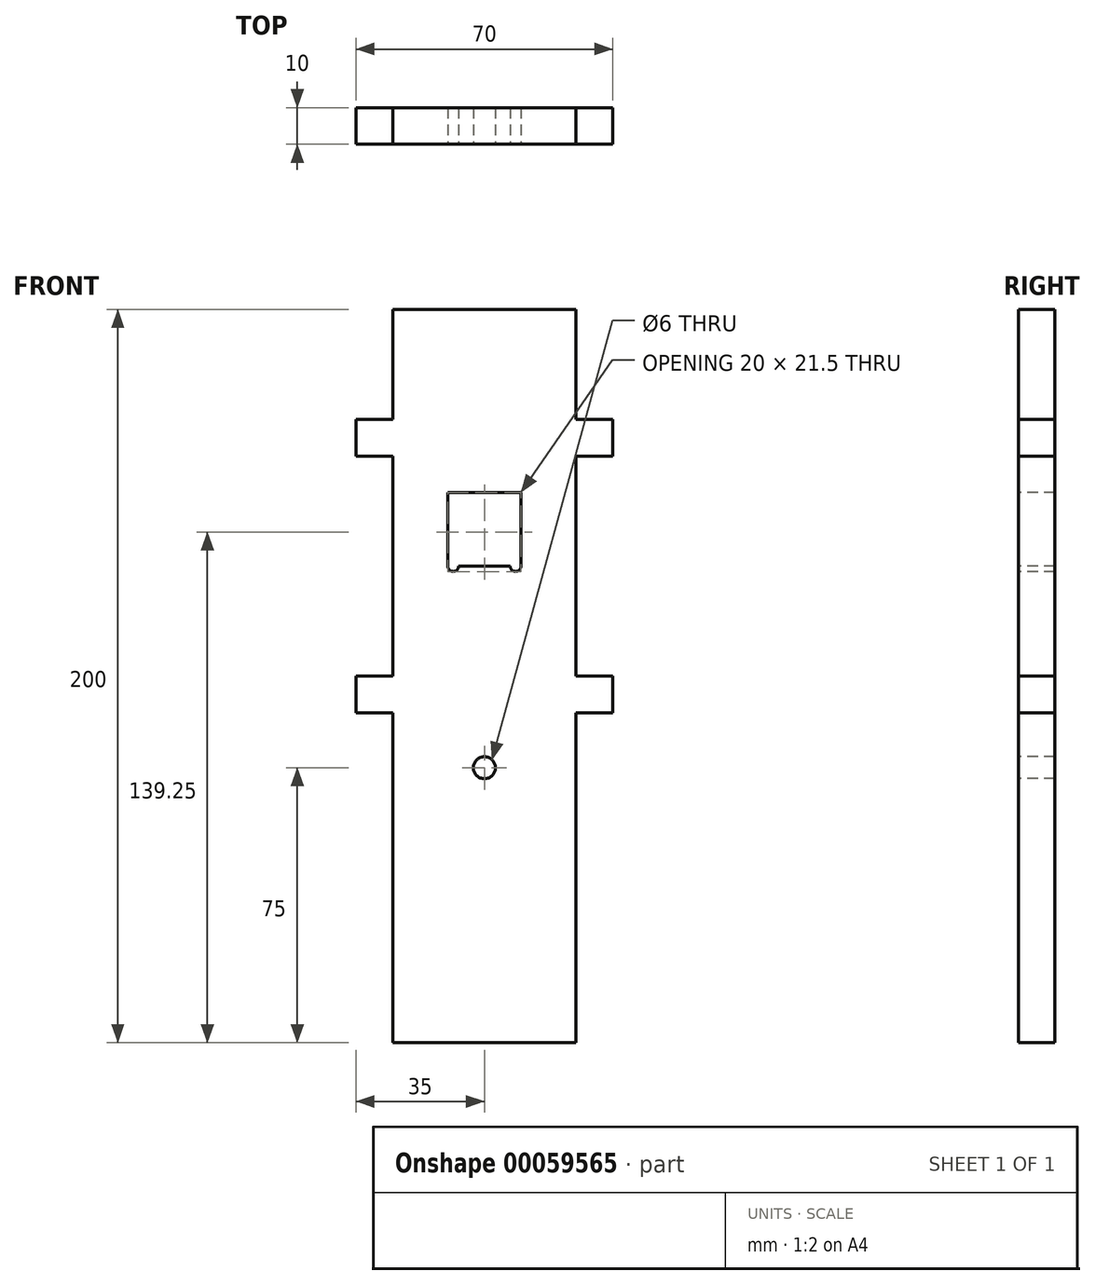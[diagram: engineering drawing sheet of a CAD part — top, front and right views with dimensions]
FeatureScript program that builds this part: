
annotation { "Feature Type Name" : "Feature", "Feature Type Description" : "" }
export const myFeature = defineFeature(function(context is Context, id is Id, definition is map)
    precondition{}
    {
        {
            var Q0;
            Q0=qCreatedBy(makeId("Front.planeOp"),FACE);
            var sketch = newSketch(context, id + "F0", { "sketchPlane" : qUnion([Q0])});
            skLineSegment(sketch, "E0.bottom", {"start": v(-25, 100) * mm, "end": v(25, 100) * mm});
            skLineSegment(sketch, "E0.top", {"start": v(-25, -100) * mm, "end": v(25, -100) * mm});
            skLineSegment(sketch, "E0.left", {"start": v(-25, 100) * mm, "end": v(-25, -100) * mm});
            skLineSegment(sketch, "E0.right", {"start": v(25, 100) * mm, "end": v(25, -100) * mm});
            skPoint(sketch, "E0.middle", {"position": v(0, 0) * mm});
            skSolve(sketch);
        }
        {
            var Q0;
            Q0 = qSketchRegion(id + "F0", true);
            extrude(context, id + "F1", {"entities" : qUnion([Q0]), "depth" : 10 * mm});
        }
        {
            var Q0;
            Q0=makeQuery(id+"F1.opExtrude","CAP_FACE",FACE,{"disambiguationData":[OSD([sQuery(id+"F0.wireOp",EDGE,"E0.bottom"),sQuery(id+"F0.wireOp",EDGE,"E0.top"),sQuery(id+"F0.wireOp",EDGE,"E0.left"),sQuery(id+"F0.wireOp",EDGE,"E0.right")])],"isStart":false});
            var sketch = newSketch(context, id + "F2", { "sketchPlane" : qUnion([Q0])});
            skCircle(sketch, "E1", {"center": v(0, -25) * mm, "radius": 3 * mm});
            skSolve(sketch);
        }
        {
            var Q0;
            Q0 = qSketchRegion(id + "F2", true);
            extrude(context, id + "F3", {"entities" : qUnion([Q0]), "operationType" : NewBodyOperationType.REMOVE, "oppositeDirection" : true, "depth" : 25 * mm});
        }
        {
            var Q0;
            Q0=makeQuery(id+"F1.opExtrude","CAP_FACE",FACE,{"disambiguationData":[OSD([sQuery(id+"F0.wireOp",EDGE,"E0.bottom"),sQuery(id+"F0.wireOp",EDGE,"E0.top"),sQuery(id+"F0.wireOp",EDGE,"E0.left"),sQuery(id+"F0.wireOp",EDGE,"E0.right")])],"isStart":false});
            var sketch = newSketch(context, id + "F4", { "sketchPlane" : qUnion([Q0])});
            skLineSegment(sketch, "E2.bottom", {"start": v(-10, 50) * mm, "end": v(10, 50) * mm});
            skLineSegment(sketch, "E2.top", {"start": v(-7, 30) * mm, "end": v(7, 30) * mm});
            skLineSegment(sketch, "E2.left", {"start": v(-10, 50) * mm, "end": v(-10, 30) * mm});
            skLineSegment(sketch, "E2.right", {"start": v(10, 50) * mm, "end": v(10, 30) * mm});
            skPoint(sketch, "E2.middle", {"position": v(0, 40) * mm});
            skArc(sketch, "E3", {"start": v(-10, 30) * mm, "mid": v(-8.5, 28.5) * mm, "end": v(-7, 30) * mm});
            skLineSegment(sketch, "E4", {"start": v(0, 30) * mm, "end": v(0, 25.67) * mm, "construction": true});
            skArc(sketch, "E5.MirrorCS", {"start": v(10, 30) * mm, "mid": v(8.5, 28.5) * mm, "end": v(7, 30) * mm});
            skSolve(sketch);
        }
        {
            var Q0;
            Q0 = qSketchRegion(id + "F4", true);
            extrude(context, id + "F5", {"entities" : qUnion([Q0]), "operationType" : NewBodyOperationType.REMOVE, "oppositeDirection" : true, "depth" : 25 * mm});
        }
        {
            var Q0;
            Q0=makeQuery(id+"F1.opExtrude","CAP_FACE",FACE,{"disambiguationData":[OSD([sQuery(id+"F0.wireOp",EDGE,"E0.bottom"),sQuery(id+"F0.wireOp",EDGE,"E0.top"),sQuery(id+"F0.wireOp",EDGE,"E0.left"),sQuery(id+"F0.wireOp",EDGE,"E0.right")])],"isStart":false});
            var sketch = newSketch(context, id + "F6", { "sketchPlane" : qUnion([Q0])});
            skLineSegment(sketch, "E6.bottom", {"start": v(-25, 70) * mm, "end": v(-35, 70) * mm});
            skLineSegment(sketch, "E6.top", {"start": v(-25, 60) * mm, "end": v(-35, 60) * mm});
            skLineSegment(sketch, "E6.left", {"start": v(-25, 70) * mm, "end": v(-25, 60) * mm});
            skLineSegment(sketch, "E6.right", {"start": v(-35, 70) * mm, "end": v(-35, 60) * mm});
            skLineSegment(sketch, "E7.MirrorCS", {"start": v(25, 70) * mm, "end": v(35, 70) * mm});
            skLineSegment(sketch, "E8.MirrorCS", {"start": v(35, 70) * mm, "end": v(35, 60) * mm});
            skLineSegment(sketch, "E9.MirrorCS", {"start": v(25, 70) * mm, "end": v(25, 60) * mm});
            skLineSegment(sketch, "E10.MirrorCS", {"start": v(25, 60) * mm, "end": v(35, 60) * mm});
            skLineSegment(sketch, "E11", {"start": v(-25, 30) * mm, "end": v(25, 30) * mm, "construction": true});
            skLineSegment(sketch, "E12.MirrorCS", {"start": v(-25, -10) * mm, "end": v(-35, -10) * mm});
            skLineSegment(sketch, "E13.MirrorCS", {"start": v(25, 0) * mm, "end": v(35, 0) * mm});
            skLineSegment(sketch, "E14.MirrorCS", {"start": v(25, -10) * mm, "end": v(35, -10) * mm});
            skLineSegment(sketch, "E15.MirrorCS", {"start": v(-25, -10) * mm, "end": v(-25, 0) * mm});
            skLineSegment(sketch, "E16.MirrorCS", {"start": v(35, -10) * mm, "end": v(35, 0) * mm});
            skLineSegment(sketch, "E17.MirrorCS", {"start": v(-25, 0) * mm, "end": v(-35, 0) * mm});
            skLineSegment(sketch, "E18.MirrorCS", {"start": v(25, -10) * mm, "end": v(25, 0) * mm});
            skLineSegment(sketch, "E19.MirrorCS", {"start": v(-35, -10) * mm, "end": v(-35, 0) * mm});
            skSolve(sketch);
        }
        {
            var Q0;
            Q0 = qSketchRegion(id + "F6", true);
            extrude(context, id + "F7", {"entities" : qUnion([Q0]), "operationType" : NewBodyOperationType.ADD, "oppositeDirection" : true, "depth" : 10 * mm});
        }
    });
